# Revit family: TY315
name_source: partatom
category: Sprinklers
revit_build: Autodesk Revit 2016 (Build: 20150220_1215(x64)
units: mm (PartAtom-declared; Revit-internal decimal feet)

## family parameters
Always vertical = Yes
Cut with Voids When Loaded = No
Maintain Annotation Orientation = No
OmniClass Number = 23.65.70.17.11.24
OmniClass Title = Fire Fighting Sprinkler Heads
Part Type = Normal
Room Calculation Point = No
Round Connector Dimension = Use Diameter
Shared = No
Work Plane-Based = No

## types (24) — shared parameters
COBie = Yes
COBie.Component.Name = Sprinklers:Upright_SIN
COBie.Type = Yes
COBie.Type.AssetType = Fixed
COBie.Type.Category = Pr_70_55_97_84:Sprinklers
COBie.Type.DurationUnit = year
COBie.Type.Manufacturer = Tyco Fire Protection Products
COBie.Type.Material = Bronze
COBie.Type.NominalHeight = 0' - 0"
COBie.Type.NominalLength = 0' - 0"
COBie.Type.NominalWidth = 0' - 0"
COBie.Type.Shape = Cylinder
COBie.Type.Size = 1/2"(DN15)
COBie.Type.WarrantyGuarantorParts = http://tycofsbp.com
Coverage = Standard
Coverage_ = Standard
K-Factor = 5.5493
Manufacturer = Tyco Fire Protection Products
Manufacturer URL = www.tyco-fire.com
Material_ = Bronze
Model = TY-B
Nominal Diameter 1 = 1"
Orifice = Standard
Orifice Size = 0"
Outside Diameter 1 = 1"
Response = Standard
Response_ = Standard
SIN No = TY315
Takeout 1 = 2"
Technical Data Sheet No = TFP152
zero-valued in all types: COBie.Type.ReplacementCost, Style Id

## per-type parameters (varying)
| type | COBie.Component.Description | COBie.Type.Colour | COBie.Type.Finish | COBie.Type.ModelNumber | COBie.Type.ModelReference | Description | Finish_ | Part No | Temperature Rating |
| Wet Upright_135  57.2°C K80 1/2"(DN15) NPT Br_77-570-1-135 | TY-B Wet Upright  57.2°C K80 DN15 NPT Br | Brass | Natural Brass | 77-570-1-135 | TY-B Wet Upright  57.2°C K80 DN15 NPT Br | TY-B Wet Upright_135  57.2°C K80 DN15 NPT Br | Natural Brass | 77-570-1-135 | 135 °F |
| Wet Upright_155  68.3°C K80 1/2"(DN15) NPT Br_77-570-1-155 | TY-B Wet Upright  68.3°C K80 DN15 NPT Br | Brass | Natural Brass | 77-570-1-155 | TY-B Wet Upright  68.3°C K80 DN15 NPT Br | TY-B Wet Upright_155  68.3°C K80 DN15 NPT Br | Natural Brass | 77-570-1-155 | 155 °F |
| Wet Upright_175  79.4°C K80 1/2"(DN15) NPT Br_77-570-1-175 | TY-B Wet Upright  79.4°C K80 DN15 NPT Br | Brass | Natural Brass | 77-570-1-175 | TY-B Wet Upright  79.4°C K80 DN15 NPT Br | TY-B Wet Upright_175  79.4°C K80 DN15 NPT Br | Natural Brass | 77-570-1-175 | 175 °F |
| Wet Upright_200  93.3°C K80 1/2"(DN15) NPT Br_77-570-1-200 | TY-B Wet Upright  93.3°C K80 DN15 NPT Br | Brass | Natural Brass | 77-570-1-200 | TY-B Wet Upright  93.3°C K80 DN15 NPT Br | TY-B Wet Upright_200  93.3°C K80 DN15 NPT Br | Natural Brass | 77-570-1-200 | 200 °F |
| Wet Upright_286  141.1°C K80 1/2"(DN15) NPT Br_77-570-1-286 | TY-B Wet Upright  141.1°C K80 DN15 NPT Br | Brass | Natural Brass | 77-570-1-286 | TY-B Wet Upright  141.1°C K80 DN15 NPT Br | TY-B Wet Upright_286  141.1°C K80 DN15 NPT Br | Natural Brass | 77-570-1-286 | 286 °F |
| Wet Upright_360  182.2°C K80 1/2"(DN15) NPT Br_77-570-1-360 | TY-B Wet Upright  182.2°C K80 DN15 NPT Br | Brass | Natural Brass | 77-570-1-360 | TY-B Wet Upright  182.2°C K80 DN15 NPT Br | TY-B Wet Upright_360  182.2°C K80 DN15 NPT Br | Natural Brass | 77-570-1-360 | 360 °F |
| Wet Upright_135  57.2°C K80 1/2"(DN15) NPT Wh9003_77-570-4-135 | TY-B Wet Upright  57.2°C K80 DN15 NPT Wh9003 | White | Signal White | 77-570-4-135 | TY-B Wet Upright  57.2°C K80 DN15 NPT Wh9003 | TY-B Wet Upright_135  57.2°C K80 DN15 NPT Wh9003 | White RAL9003 | 77-570-4-135 | 135 °F |
| Wet Upright_155  68.3°C K80 1/2"(DN15) NPT Wh9003_77-570-4-155 | TY-B Wet Upright  68.3°C K80 DN15 NPT Wh9003 | White | Signal White | 77-570-4-155 | TY-B Wet Upright  68.3°C K80 DN15 NPT Wh9003 | TY-B Wet Upright_155  68.3°C K80 DN15 NPT Wh9003 | White RAL9003 | 77-570-4-155 | 155 °F |
| Wet Upright_175  79.4°C K80 1/2"(DN15) NPT Wh9003_77-570-4-175 | TY-B Wet Upright  79.4°C K80 DN15 NPT Wh9003 | White | Signal White | 77-570-4-175 | TY-B Wet Upright  79.4°C K80 DN15 NPT Wh9003 | TY-B Wet Upright_175  79.4°C K80 DN15 NPT Wh9003 | White RAL9003 | 77-570-4-175 | 175 °F |
| Wet Upright_200  93.3°C K80 1/2"(DN15) NPT Wh9003_77-570-4-200 | TY-B Wet Upright  93.3°C K80 DN15 NPT Wh9003 | White | Signal White | 77-570-4-200 | TY-B Wet Upright  93.3°C K80 DN15 NPT Wh9003 | TY-B Wet Upright_200  93.3°C K80 DN15 NPT Wh9003 | White RAL9003 | 77-570-4-200 | 200 °F |
| Wet Upright_286  141.1°C K80 1/2"(DN15) NPT Wh9003_77-570-4-286 | TY-B Wet Upright  141.1°C K80 DN15 NPT Wh9003 | White | Signal White | 77-570-4-286 | TY-B Wet Upright  141.1°C K80 DN15 NPT Wh9003 | TY-B Wet Upright_286  141.1°C K80 DN15 NPT Wh9003 | White RAL9003 | 77-570-4-286 | 286 °F |
| Wet Upright_360  182.2°C K80 1/2"(DN15) NPT Wh9003_77-570-4-360 | TY-B Wet Upright  182.2°C K80 DN15 NPT Wh9003 | White | Signal White | 77-570-4-360 | TY-B Wet Upright  182.2°C K80 DN15 NPT Wh9003 | TY-B Wet Upright_360  182.2°C K80 DN15 NPT Wh9003 | White RAL9003 | 77-570-4-360 | 360 °F |
| Wet Upright_135  57.2°C K80 1/2"(DN15) NPT Wh9003_77-570-5-135 | TY-B Wet Upright_135  57.2°C K80 DN15 NPT Wh9003 | Black | Jet Black | 77-570-5-135 | TY-B Wet Upright_135  57.2°C K80 DN15 NPT Wh9003 | TY-B Wet Upright_135  57.2°C K80 DN15 NPT Wh9003 | White RAL9003 | 77-570-5-135 | 135 °F |
| Wet Upright_155  57.2°C K80 1/2"(DN15) NPT Wh9003_77-570-5-155 | TY-B Wet Upright_135  57.2°C K80 DN15 NPT Wh9003 | Black | Jet Black | 77-570-5-155 | TY-B Wet Upright_135  57.2°C K80 DN15 NPT Wh9003 | TY-B Wet Upright_155  57.2°C K80 DN15 NPT Wh9003 | White RAL9003 | 77-570-5-155 | 135 °F |
| Wet Upright_175  57.2°C K80 1/2"(DN15) NPT Wh9003_77-570-5-175 | TY-B Wet Upright_155  57.2°C K80 DN15 NPT Wh9003 | Black | Jet Black | 77-570-5-175 | TY-B Wet Upright_155  57.2°C K80 DN15 NPT Wh9003 | TY-B Wet Upright_175  57.2°C K80 DN15 NPT Wh9003 | White RAL9003 | 77-570-5-175 | 135 °F |
| Wet Upright_200  57.2°C K80 1/2"(DN15) NPT Wh9003_77-570-5-200 | TY-B Wet Upright_175  57.2°C K80 DN15 NPT Wh9003 | Black | Jet Black | 77-570-5-200 | TY-B Wet Upright_175  57.2°C K80 DN15 NPT Wh9003 | TY-B Wet Upright_200  57.2°C K80 DN15 NPT Wh9003 | White RAL9003 | 77-570-5-200 | 135 °F |
| Wet Upright_286  57.2°C K80 1/2"(DN15) NPT Wh9003_77-570-5-286 | TY-B Wet Upright_200  57.2°C K80 DN15 NPT Wh9003 | Black | Jet Black | 77-570-5-286 | TY-B Wet Upright_200  57.2°C K80 DN15 NPT Wh9003 | TY-B Wet Upright_286  57.2°C K80 DN15 NPT Wh9003 | White RAL9003 | 77-570-5-286 | 135 °F |
| Wet Upright_360  57.2°C K80 1/2"(DN15) NPT Wh9003_77-570-5-360 | TY-B Wet Upright_286  57.2°C K80 DN15 NPT Wh9003 | Black | Jet Black | 77-570-5-360 | TY-B Wet Upright_286  57.2°C K80 DN15 NPT Wh9003 | TY-B Wet Upright_360  57.2°C K80 DN15 NPT Wh9003 | White RAL9003 | 77-570-5-360 | 135 °F |
| Wet Upright_135  57.2°C K80 1/2"(DN15) NPT Chr_77-570-9-135 | TY-B Wet Upright  57.2°C K80 DN15 NPT Chr | Silver | Chrome Plated | 77-570-9-135 | TY-B Wet Upright  57.2°C K80 DN15 NPT Chr | TY-B Wet Upright_135  57.2°C K80 DN15 NPT Chr | Chrome Plated | 77-570-9-135 | 135 °F |
| Wet Upright_155  68.3°C K80 1/2"(DN15) NPT Chr_77-570-9-155 | TY-B Wet Upright  68.3°C K80 DN15 NPT Chr | Silver | Chrome Plated | 77-570-9-155 | TY-B Wet Upright  68.3°C K80 DN15 NPT Chr | TY-B Wet Upright_155  68.3°C K80 DN15 NPT Chr | Chrome Plated | 77-570-9-155 | 155 °F |
| Wet Upright_175  79.4°C K80 1/2"(DN15) NPT Chr_77-570-9-175 | TY-B Wet Upright  79.4°C K80 DN15 NPT Chr | Silver | Chrome Plated | 77-570-9-175 | TY-B Wet Upright  79.4°C K80 DN15 NPT Chr | TY-B Wet Upright_175  79.4°C K80 DN15 NPT Chr | Chrome Plated | 77-570-9-175 | 175 °F |
| Wet Upright_200  93.3°C K80 1/2"(DN15) NPT Chr_77-570-9-200 | TY-B Wet Upright  93.3°C K80 DN15 NPT Chr | Silver | Chrome Plated | 77-570-9-200 | TY-B Wet Upright  93.3°C K80 DN15 NPT Chr | TY-B Wet Upright_200  93.3°C K80 DN15 NPT Chr | Chrome Plated | 77-570-9-200 | 200 °F |
| Wet Upright_286  141.1°C K80 1/2"(DN15) NPT Chr_77-570-9-286 | TY-B Wet Upright  141.1°C K80 DN15 NPT Chr | Silver | Chrome Plated | 77-570-9-286 | TY-B Wet Upright  141.1°C K80 DN15 NPT Chr | TY-B Wet Upright_286  141.1°C K80 DN15 NPT Chr | Chrome Plated | 77-570-9-286 | 286 °F |
| Wet Upright_360  182.2°C K80 1/2"(DN15) NPT Chr_77-570-9-360 | TY-B Wet Upright  182.2°C K80 DN15 NPT Chr | Silver | Chrome Plated | 77-570-9-360 | TY-B Wet Upright  182.2°C K80 DN15 NPT Chr | TY-B Wet Upright_360  182.2°C K80 DN15 NPT Chr | Chrome Plated | 77-570-9-360 | 360 °F |

## geometry (parser evidence)
native form markers: Blend x2, Sweep x59
no freeform markers — native parametric forms only
